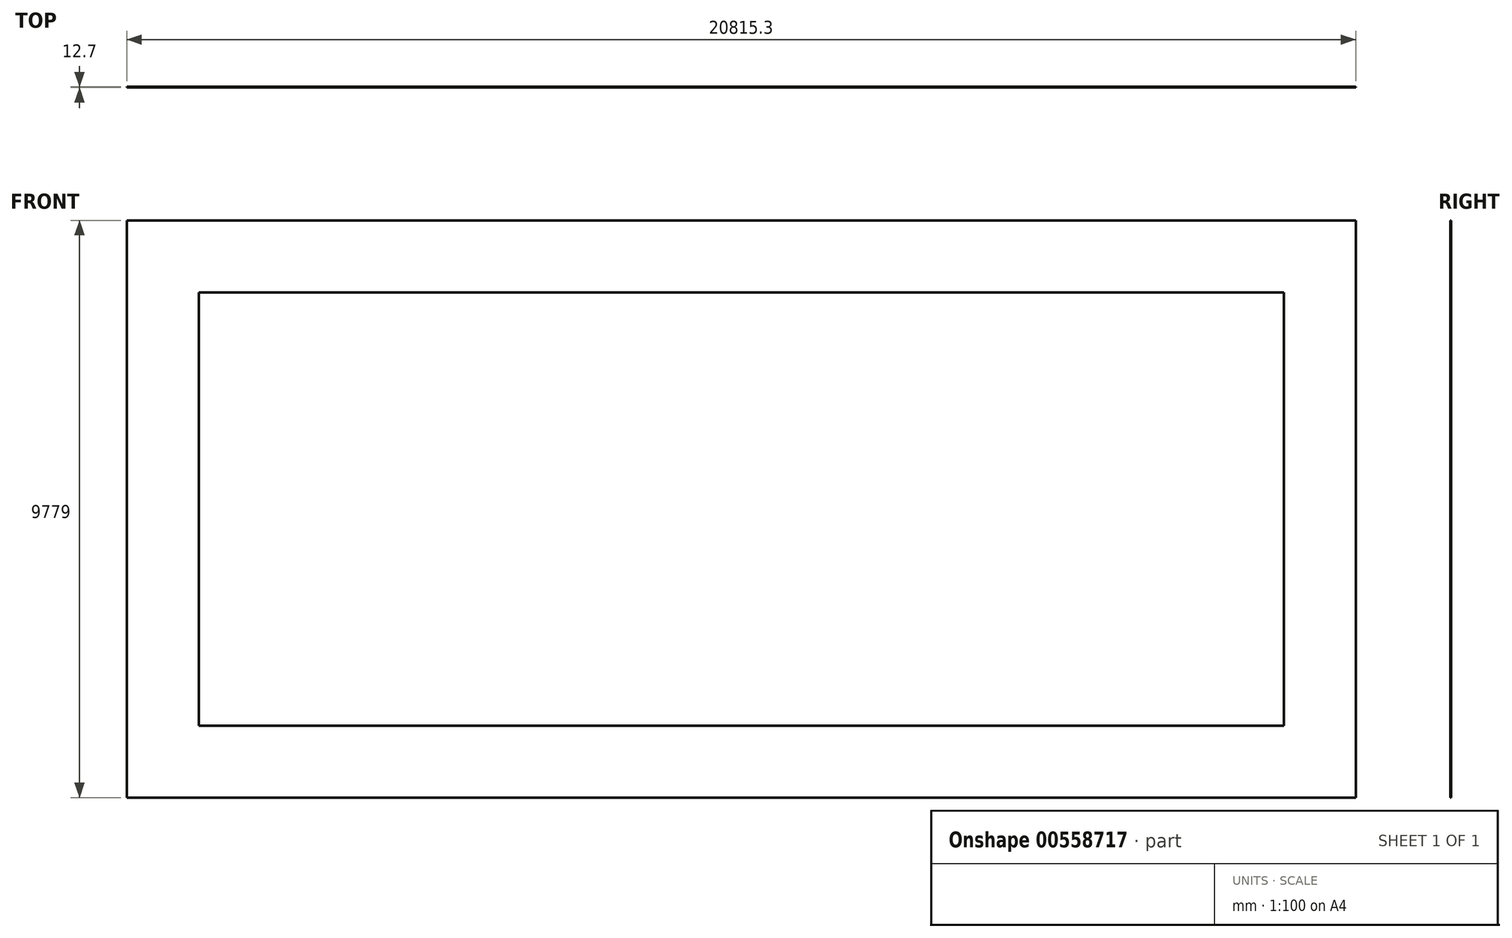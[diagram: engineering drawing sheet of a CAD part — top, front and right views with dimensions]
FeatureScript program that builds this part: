
annotation { "Feature Type Name" : "Feature", "Feature Type Description" : "" }
export const myFeature = defineFeature(function(context is Context, id is Id, definition is map)
    precondition{}
    {
        {
            var Q0;
            Q0=qCreatedBy(makeId("Front.planeOp"),FACE);
            var sketch = newSketch(context, id + "F0", { "sketchPlane" : qUnion([Q0])});
            skLineSegment(sketch, "E0.bottom", {"start": v(0, 0) * mm, "end": v(20815.3, 0) * mm});
            skLineSegment(sketch, "E0.top", {"start": v(0, 9779) * mm, "end": v(20815.3, 9779) * mm});
            skLineSegment(sketch, "E0.left", {"start": v(0, 0) * mm, "end": v(0, 9779) * mm});
            skLineSegment(sketch, "E0.right", {"start": v(20815.3, 0) * mm, "end": v(20815.3, 9779) * mm});
            skLineSegment(sketch, "E1.0", {"start": v(1219.2, 8559.8) * mm, "end": v(19596.1, 8559.8) * mm});
            skLineSegment(sketch, "E1.1", {"start": v(1219.2, 1219.2) * mm, "end": v(1219.2, 8559.8) * mm});
            skLineSegment(sketch, "E1.2", {"start": v(1219.2, 1219.2) * mm, "end": v(19596.1, 1219.2) * mm});
            skLineSegment(sketch, "E1.3", {"start": v(19596.1, 1219.2) * mm, "end": v(19596.1, 8559.8) * mm});
            skSolve(sketch);
        }
        {
            var Q0;
            Q0 = qSketchRegion(id + "F0", true);
            extrude(context, id + "F1", {"entities" : qUnion([Q0]), "depth" : 12.7 * mm, "offsetDistance" : 25.4 * mm});
        }
    });
